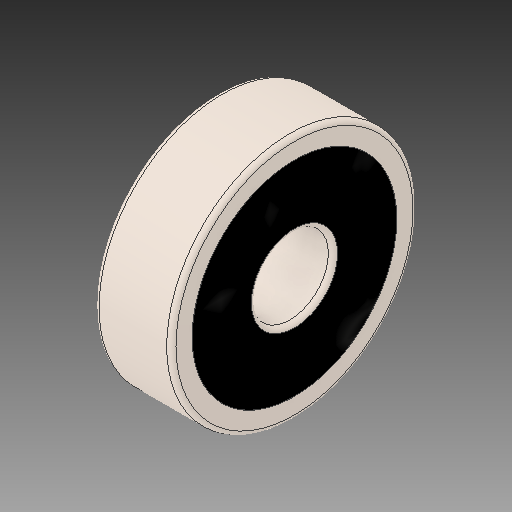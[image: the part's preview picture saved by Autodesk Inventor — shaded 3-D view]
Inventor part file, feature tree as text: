
AUTODESK INVENTOR PART (.ipt)
format: ipt  version: 2017 (Build 210142000, 142)  size: 2,315,776 bytes
history: imported  units: mm
features: other x22, sketch x2, imported_body x1
ambient origin geometry x8: Origin, YZ Plane, XZ Plane, XY Plane, X Axis, Y Axis, Z Axis, Center Point
bodies: Solid1 (imported_parasolid), Solid2 (imported_parasolid), Solid3 (imported_parasolid), Solid4 (imported_parasolid), Solid5 (imported_parasolid), Solid6 (imported_parasolid), Solid7 (imported_parasolid), Solid8 (imported_parasolid), Solid9 (imported_parasolid), Solid10 (imported_parasolid), Solid11 (imported_parasolid), Solid12 (imported_parasolid), Solid13 (imported_parasolid), Solid14 (imported_parasolid), Solid15 (imported_parasolid), Solid16 (imported_parasolid), Solid17 (imported_parasolid), Solid18 (imported_parasolid), Solid19 (imported_parasolid), Solid20 (imported_parasolid)
feature tree (25):
  other  "SKF 625_CPY_MIR1.ipt"
  other  "Solid1::SKF 625_CPY_MIR1.ipt"
  other  "Solid2::SKF 625_CPY_MIR1.ipt"
  other  "Solid3::SKF 625_CPY_MIR1.ipt"
  other  "Solid4::SKF 625_CPY_MIR1.ipt"
  other  "Solid5::SKF 625_CPY_MIR1.ipt"
  other  "Solid6::SKF 625_CPY_MIR1.ipt"
  other  "Solid7::SKF 625_CPY_MIR1.ipt"
  other  "Solid8::SKF 625_CPY_MIR1.ipt"
  other  "Solid9::SKF 625_CPY_MIR1.ipt"
  other  "Solid10::SKF 625_CPY_MIR1.ipt"
  other  "Solid11::SKF 625_CPY_MIR1.ipt"
  other  "Solid12::SKF 625_CPY_MIR1.ipt"
  other  "Solid13::SKF 625_CPY_MIR1.ipt"
  other  "Solid14::SKF 625_CPY_MIR1.ipt"
  other  "Solid15::SKF 625_CPY_MIR1.ipt"
  other  "Solid16::SKF 625_CPY_MIR1.ipt"
  other  "Solid17::SKF 625_CPY_MIR1.ipt"
  other  "Solid18::SKF 625_CPY_MIR1.ipt"
  other  "Solid19::SKF 625_CPY_MIR1.ipt"
  other  "Solid20::SKF 625_CPY_MIR1.ipt"
  other  "TaggingFeature1"
  sketch  "Sketch1"  dims[d0=10.0mm]
  sketch  "Sketch2"
  imported_body  NMx_Import_Brep_tag  [imported B-rep: ~49 faces, bbox_mm=None]
